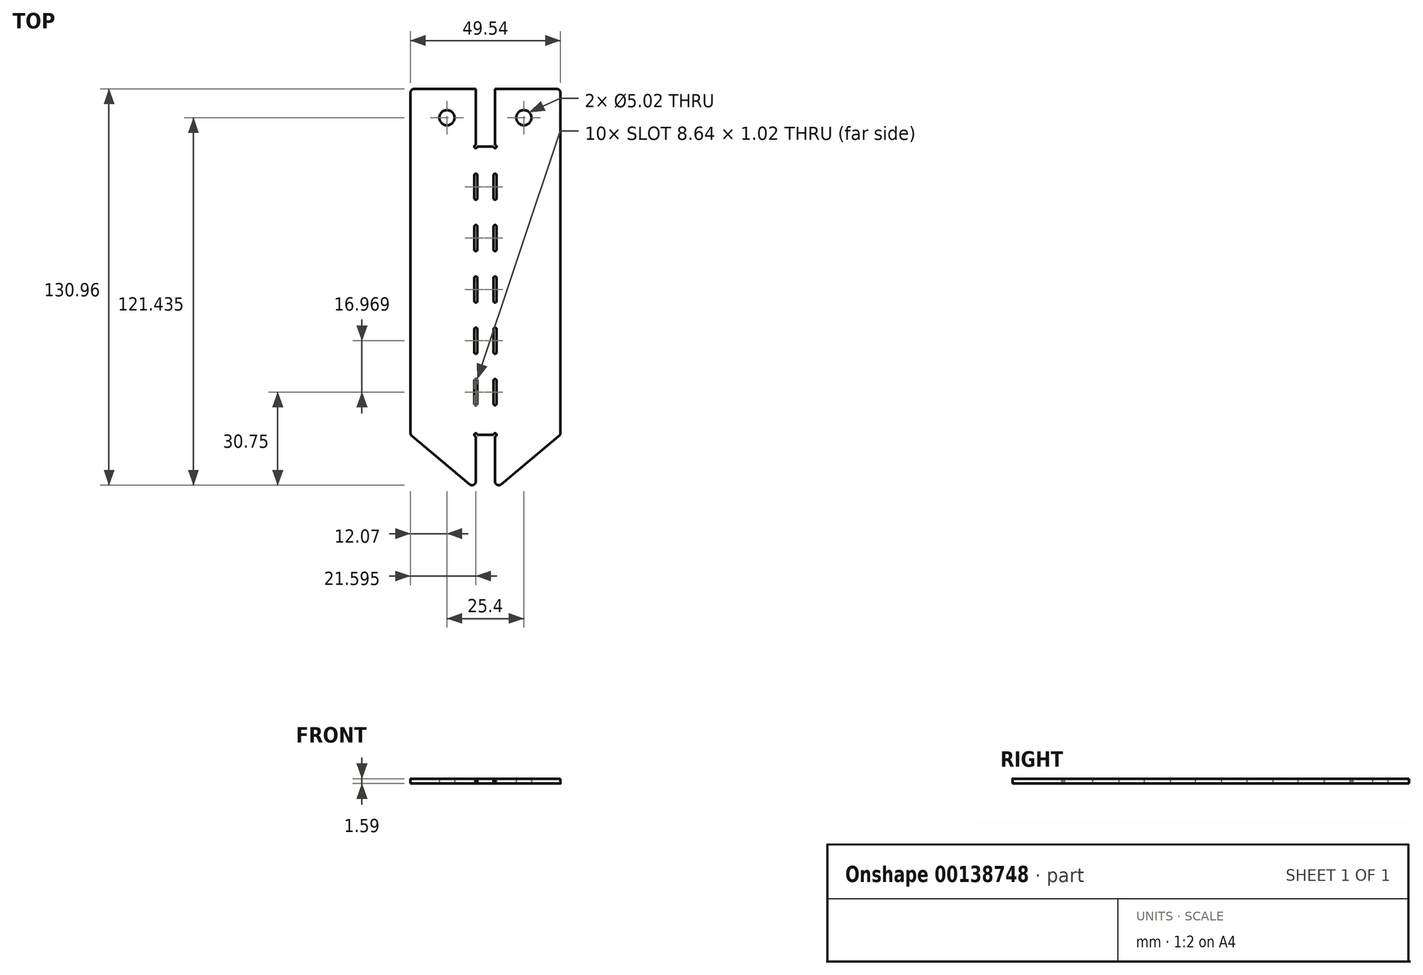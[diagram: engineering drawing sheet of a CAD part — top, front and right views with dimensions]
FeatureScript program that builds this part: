
annotation { "Feature Type Name" : "Feature", "Feature Type Description" : "" }
export const myFeature = defineFeature(function(context is Context, id is Id, definition is map)
    precondition{}
    {
        {
            var Q0;
            Q0=qCreatedBy(makeId("Top.planeOp"),FACE);
            var sketch = newSketch(context, id + "F0", { "sketchPlane" : qUnion([Q0])});
            skLineSegment(sketch, "E0", {"start": v(0, 0) * mm, "end": v(0, 95.25) * mm, "construction": true});
            skLineSegment(sketch, "E1", {"start": v(0, 95.25) * mm, "end": v(-2.67, 95.25) * mm});
            skLineSegment(sketch, "E2", {"start": v(-3.18, 95.76) * mm, "end": v(-3.18, 114.3) * mm});
            skLineSegment(sketch, "E3", {"start": v(-3.18, 114.3) * mm, "end": v(-24.77, 114.3) * mm});
            skLineSegment(sketch, "E4", {"start": v(-24.77, 114.3) * mm, "end": v(-24.76, 0) * mm});
            skLineSegment(sketch, "E5", {"start": v(-2.67, 0) * mm, "end": v(0, 0) * mm});
            skCircle(sketch, "E6", {"center": v(-12.7, 104.78) * mm, "radius": 2.5 * mm});
            skLineSegment(sketch, "E7", {"start": v(-3.18, 95.25) * mm, "end": v(-3.17, 0) * mm, "construction": true});
            skLineSegment(sketch, "E8.left", {"start": v(-3.68, 51.84) * mm, "end": v(-3.68, 44.22) * mm});
            skLineSegment(sketch, "E8.right", {"start": v(-2.67, 51.84) * mm, "end": v(-2.67, 44.22) * mm});
            skPoint(sketch, "E8.middle", {"position": v(-3.18, 48.03) * mm});
            skArc(sketch, "E9", {"start": v(-3.68, 51.84) * mm, "mid": v(-3.18, 52.35) * mm, "end": v(-2.67, 51.84) * mm});
            skArc(sketch, "E10", {"start": v(-3.68, 44.22) * mm, "mid": v(-3.17, 43.7) * mm, "end": v(-2.67, 44.22) * mm});
            skPoint(sketch, "E11.0.1.0", {"position": v(-3.18, 31.06) * mm});
            skLineSegment(sketch, "E11.0.1.1", {"start": v(-2.67, 34.87) * mm, "end": v(-2.67, 27.25) * mm});
            skLineSegment(sketch, "E11.0.1.2", {"start": v(-3.68, 34.87) * mm, "end": v(-3.68, 27.25) * mm});
            skArc(sketch, "E11.0.1.3", {"start": v(-3.68, 34.87) * mm, "mid": v(-3.18, 35.38) * mm, "end": v(-2.67, 34.87) * mm});
            skArc(sketch, "E11.0.1.4", {"start": v(-3.68, 27.25) * mm, "mid": v(-3.17, 26.74) * mm, "end": v(-2.67, 27.25) * mm});
            skPoint(sketch, "E11.0.2.0", {"position": v(-3.18, 14.09) * mm});
            skLineSegment(sketch, "E11.0.2.1", {"start": v(-2.67, 17.9) * mm, "end": v(-2.67, 10.28) * mm});
            skLineSegment(sketch, "E11.0.2.2", {"start": v(-3.68, 17.9) * mm, "end": v(-3.68, 10.28) * mm});
            skArc(sketch, "E11.0.2.3", {"start": v(-3.68, 17.9) * mm, "mid": v(-3.18, 18.4) * mm, "end": v(-2.67, 17.9) * mm});
            skArc(sketch, "E11.0.2.4", {"start": v(-3.68, 10.28) * mm, "mid": v(-3.17, 9.77) * mm, "end": v(-2.67, 10.28) * mm});
            skLineSegment(sketch, "E11.direction1", {"start": v(-3.68, 44.22) * mm, "end": v(21.72, 44.22) * mm, "construction": true});
            skLineSegment(sketch, "E11.direction2", {"start": v(-3.68, 44.22) * mm, "end": v(-3.68, 27.25) * mm, "construction": true});
            skArc(sketch, "E12.MirrorCS", {"start": v(3.68, 44.22) * mm, "mid": v(3.17, 43.7) * mm, "end": v(2.67, 44.22) * mm});
            skArc(sketch, "E13.MirrorCS", {"start": v(3.68, 27.25) * mm, "mid": v(3.17, 26.74) * mm, "end": v(2.67, 27.25) * mm});
            skArc(sketch, "E14.MirrorCS", {"start": v(3.68, 10.28) * mm, "mid": v(3.17, 9.77) * mm, "end": v(2.67, 10.28) * mm});
            skArc(sketch, "E15.MirrorCS", {"start": v(3.68, 34.87) * mm, "mid": v(3.18, 35.38) * mm, "end": v(2.67, 34.87) * mm});
            skArc(sketch, "E16.MirrorCS", {"start": v(3.68, 51.84) * mm, "mid": v(3.18, 52.35) * mm, "end": v(2.67, 51.84) * mm});
            skArc(sketch, "E17.MirrorCS", {"start": v(3.68, 17.9) * mm, "mid": v(3.18, 18.4) * mm, "end": v(2.67, 17.9) * mm});
            skLineSegment(sketch, "E18.MirrorCS", {"start": v(2.67, 0) * mm, "end": v(0, 0) * mm});
            skLineSegment(sketch, "E19.MirrorCS", {"start": v(0, 95.25) * mm, "end": v(2.67, 95.25) * mm});
            skLineSegment(sketch, "E20.MirrorCS", {"start": v(3.68, 17.9) * mm, "end": v(3.68, 10.28) * mm});
            skLineSegment(sketch, "E21.MirrorCS", {"start": v(2.67, 51.84) * mm, "end": v(2.67, 44.22) * mm});
            skLineSegment(sketch, "E22.MirrorCS", {"start": v(3.68, 51.84) * mm, "end": v(3.68, 44.22) * mm});
            skLineSegment(sketch, "E23.MirrorCS", {"start": v(2.67, 34.87) * mm, "end": v(2.67, 27.25) * mm});
            skLineSegment(sketch, "E24.MirrorCS", {"start": v(2.67, 17.9) * mm, "end": v(2.67, 10.28) * mm});
            skLineSegment(sketch, "E25.MirrorCS", {"start": v(3.68, 34.87) * mm, "end": v(3.68, 27.25) * mm});
            skLineSegment(sketch, "E26.MirrorCS", {"start": v(3.68, 44.22) * mm, "end": v(3.68, 27.25) * mm, "construction": true});
            skLineSegment(sketch, "E27.MirrorCS", {"start": v(3.18, 95.25) * mm, "end": v(3.17, 0) * mm, "construction": true});
            skCircle(sketch, "E28.MirrorC", {"center": v(12.7, 104.78) * mm, "radius": 2.5 * mm});
            skPoint(sketch, "E29.MirrorP", {"position": v(3.18, 31.06) * mm});
            skLineSegment(sketch, "E30.MirrorCS", {"start": v(24.77, 114.3) * mm, "end": v(24.76, 0) * mm});
            skLineSegment(sketch, "E31.MirrorCS", {"start": v(3.68, 44.22) * mm, "end": v(-21.72, 44.22) * mm, "construction": true});
            skLineSegment(sketch, "E32.MirrorCS", {"start": v(3.18, 95.76) * mm, "end": v(3.18, 114.3) * mm});
            skLineSegment(sketch, "E33.MirrorCS", {"start": v(3.18, 114.3) * mm, "end": v(24.77, 114.3) * mm});
            skPoint(sketch, "E34.MirrorP", {"position": v(3.18, 48.03) * mm});
            skPoint(sketch, "E35.MirrorP", {"position": v(3.18, 14.09) * mm});
            skArc(sketch, "E36", {"start": v(-3.18, 95.76) * mm, "mid": v(-3.53, 94.9) * mm, "end": v(-2.67, 95.25) * mm});
            skArc(sketch, "E37", {"start": v(-2.67, 0) * mm, "mid": v(-3.53, 0.36) * mm, "end": v(-3.17, -0.5) * mm});
            skArc(sketch, "E38.MirrorCS", {"start": v(2.67, 0) * mm, "mid": v(3.35, 0.48) * mm, "end": v(3.56, -0.33) * mm});
            skArc(sketch, "E39.MirrorCS", {"start": v(3.18, 95.76) * mm, "mid": v(3.53, 94.9) * mm, "end": v(2.67, 95.25) * mm});
            skLineSegment(sketch, "E40", {"start": v(-24.77, 0) * mm, "end": v(-5.26, -16.37) * mm});
            skLineSegment(sketch, "E41", {"start": v(-3.17, -15.4) * mm, "end": v(-3.17, -0.5) * mm});
            skPoint(sketch, "E42.orphan", {"position": v(-3.56, -0.33) * mm});
            skLineSegment(sketch, "E43.MirrorCS", {"start": v(3.17, -15.4) * mm, "end": v(3.17, -0.5) * mm});
            skLineSegment(sketch, "E44.MirrorCS", {"start": v(24.77, 0) * mm, "end": v(5.26, -16.37) * mm});
            skArc(sketch, "E45.MirrorCS", {"start": v(2.67, 0) * mm, "mid": v(3.53, 0.36) * mm, "end": v(3.17, -0.5) * mm});
            skArc(sketch, "E46.filletArc", {"start": v(-5.26, -16.37) * mm, "mid": v(-3.9, -16.54) * mm, "end": v(-3.18, -15.4) * mm});
            skArc(sketch, "E47.filletArc", {"start": v(3.18, -15.4) * mm, "mid": v(3.9, -16.54) * mm, "end": v(5.26, -16.37) * mm});
            skLineSegment(sketch, "E48.0.1.0", {"start": v(-2.67, 68.8) * mm, "end": v(-2.67, 61.18) * mm});
            skArc(sketch, "E48.0.1.1", {"start": v(-3.68, 68.8) * mm, "mid": v(-3.18, 69.31) * mm, "end": v(-2.67, 68.8) * mm});
            skLineSegment(sketch, "E48.0.1.2", {"start": v(-3.68, 68.8) * mm, "end": v(-3.68, 61.18) * mm});
            skArc(sketch, "E48.0.1.3", {"start": v(-3.68, 61.18) * mm, "mid": v(-3.17, 60.68) * mm, "end": v(-2.67, 61.18) * mm});
            skArc(sketch, "E48.0.1.4", {"start": v(3.68, 61.18) * mm, "mid": v(3.17, 60.68) * mm, "end": v(2.67, 61.18) * mm});
            skLineSegment(sketch, "E48.0.1.5", {"start": v(2.67, 68.8) * mm, "end": v(2.67, 61.18) * mm});
            skLineSegment(sketch, "E48.0.1.6", {"start": v(3.68, 68.8) * mm, "end": v(3.68, 61.18) * mm});
            skArc(sketch, "E48.0.1.7", {"start": v(3.68, 68.8) * mm, "mid": v(3.18, 69.31) * mm, "end": v(2.67, 68.8) * mm});
            skLineSegment(sketch, "E48.0.2.0", {"start": v(-2.67, 85.77) * mm, "end": v(-2.67, 78.15) * mm});
            skArc(sketch, "E48.0.2.1", {"start": v(-3.68, 85.77) * mm, "mid": v(-3.18, 86.28) * mm, "end": v(-2.67, 85.77) * mm});
            skLineSegment(sketch, "E48.0.2.2", {"start": v(-3.68, 85.77) * mm, "end": v(-3.68, 78.15) * mm});
            skArc(sketch, "E48.0.2.3", {"start": v(-3.68, 78.15) * mm, "mid": v(-3.17, 77.64) * mm, "end": v(-2.67, 78.15) * mm});
            skArc(sketch, "E48.0.2.4", {"start": v(3.68, 78.15) * mm, "mid": v(3.17, 77.64) * mm, "end": v(2.67, 78.15) * mm});
            skLineSegment(sketch, "E48.0.2.5", {"start": v(2.67, 85.77) * mm, "end": v(2.67, 78.15) * mm});
            skLineSegment(sketch, "E48.0.2.6", {"start": v(3.68, 85.77) * mm, "end": v(3.68, 78.15) * mm});
            skArc(sketch, "E48.0.2.7", {"start": v(3.68, 85.77) * mm, "mid": v(3.18, 86.28) * mm, "end": v(2.67, 85.77) * mm});
            skLineSegment(sketch, "E48.direction1", {"start": v(-2.67, 44.22) * mm, "end": v(22.73, 44.22) * mm, "construction": true});
            skLineSegment(sketch, "E48.direction2", {"start": v(-2.67, 44.22) * mm, "end": v(-2.67, 61.18) * mm, "construction": true});
            skSolve(sketch);
        }
        {
            var Q0;
            Q0=makeQuery(id+"F0.imprint","IMPRINT",FACE,{"disambiguationData":[TD([[makeQuery(id+"F0.imprint","IMPRINT",EDGE,{"derivedFrom":sQuery(id+"F0.wireOp",EDGE,"E1")}),1.0]])]});
            extrude(context, id + "F1", {"entities" : qUnion([Q0]), "depth" : 1.59 * mm});
        }
        {
            var Q0;
            Q0=makeQuery(id+"F1.opExtrude","SWEPT_EDGE",EDGE,{"disambiguationData":[OSD([sQuery(id+"F0.wireOp",EDGE,"E4"),sQuery(id+"F0.wireOp",EDGE,"jD8TGMHM-EPRn-vw7c-2Qjf-o6hNF1Aji3Qc")])]});
            var Q1;
            Q1=makeQuery(id+"F1.opExtrude","SWEPT_EDGE",EDGE,{"disambiguationData":[OSD([sQuery(id+"F0.wireOp",EDGE,"E138.MirrorCS"),sQuery(id+"F0.wireOp",EDGE,"E30.MirrorCS")])]});
            fillet(context, id + "F2", {"entities" : qUnion([Q0, Q1]), "radius" : 1.27 * mm, "tangentPropagation" : true, "allowEdgeOverflow" : false});
        }
    });
